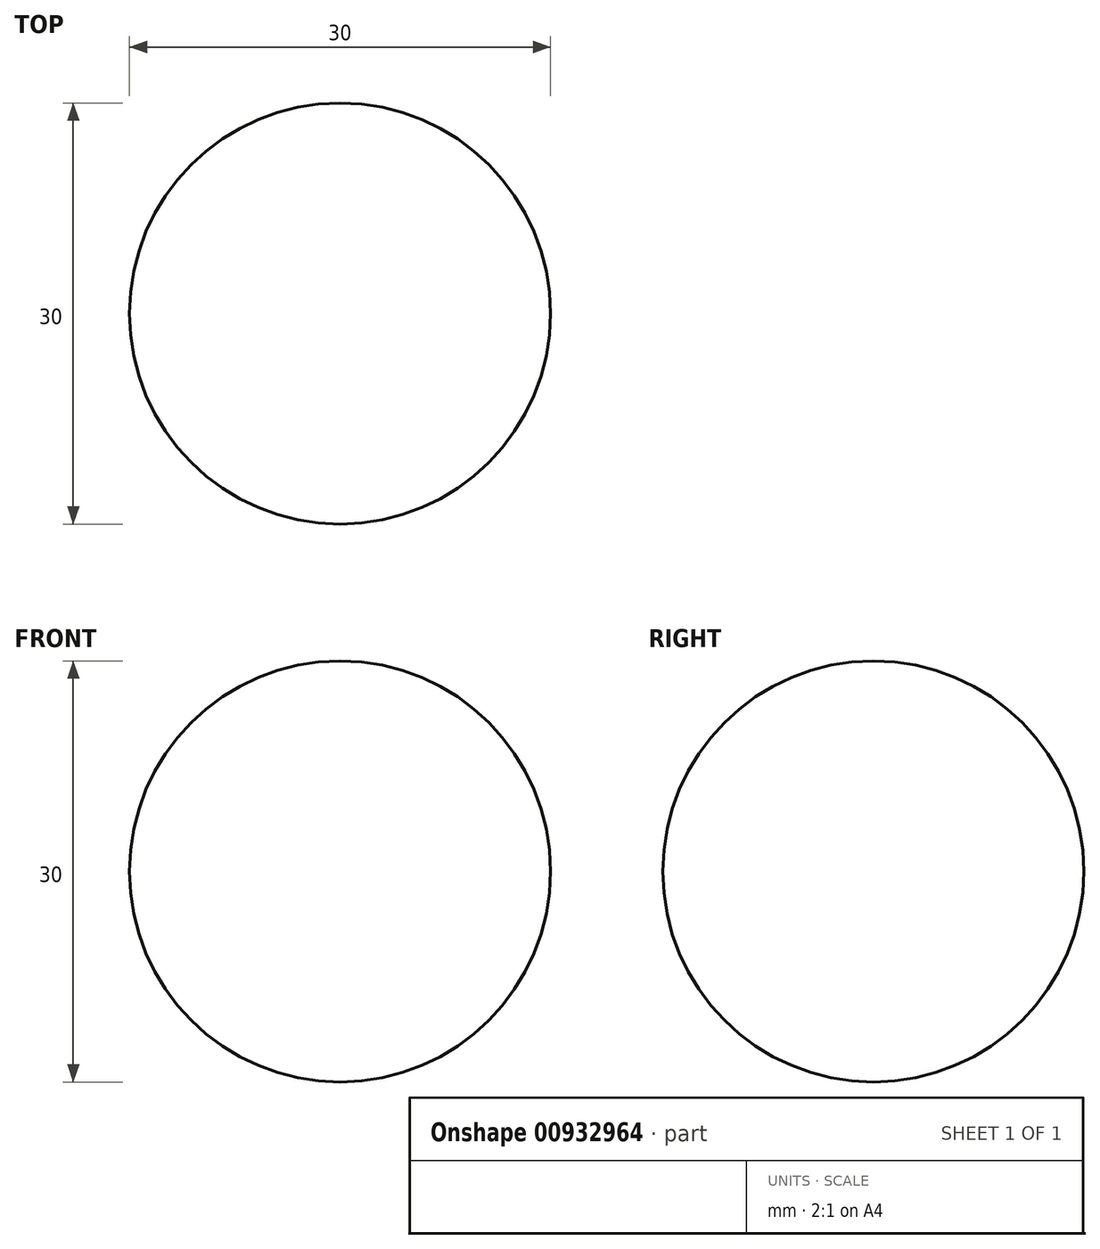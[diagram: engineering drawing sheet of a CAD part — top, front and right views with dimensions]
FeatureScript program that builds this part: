
annotation { "Feature Type Name" : "Feature", "Feature Type Description" : "" }
export const myFeature = defineFeature(function(context is Context, id is Id, definition is map)
    precondition{}
    {
        {
            var Q0;
            Q0=qCreatedBy(makeId("Top.planeOp"),FACE);
            var sketch = newSketch(context, id + "F0", { "sketchPlane" : qUnion([Q0])});
            skCircle(sketch, "E0", {"center": v(0, 0) * mm, "radius": 15 * mm});
            skSolve(sketch);
        }
        {
            var Q0;
            Q0=makeQuery(id+"F0.imprint","IMPRINT",FACE,{"disambiguationData":[TD([[makeQuery(id+"F0.imprint","IMPRINT",EDGE,{"derivedFrom":sQuery(id+"F0.wireOp",EDGE,"E0")}),1.0]])]});
            extrude(context, id + "F1", {"entities" : qUnion([Q0]), "endBound" : BoundingType.SYMMETRIC, "oppositeDirection" : true, "depth" : 30 * mm, "offsetDistance" : 25 * mm});
        }
        {
            var Q0;
            Q0=makeQuery(id+"F1.opExtrude","CAP_EDGE",EDGE,{"disambiguationData":[OSD([sQuery(id+"F0.wireOp",EDGE,"E0")])],"isStart":true});
            var Q1;
            Q1=makeQuery(id+"F1.opExtrude","CAP_EDGE",EDGE,{"disambiguationData":[OSD([sQuery(id+"F0.wireOp",EDGE,"E0")])],"isStart":false});
            fillet(context, id + "F2", {"entities" : qUnion([Q0, Q1]), "radius" : 15 * mm, "tangentPropagation" : true, "allowEdgeOverflow" : false});
        }
    });
